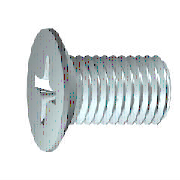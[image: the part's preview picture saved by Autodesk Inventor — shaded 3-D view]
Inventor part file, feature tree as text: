
AUTODESK INVENTOR PART (.ipt)
format: ipt  version: 2022 (Build 260153000, 153)  size: 241,664 bytes
history: native  units: mm (DEFAULTED — no unit token found)
features: sketch x1, extrude x1, plane x1
ambient origin geometry x7: Origin, YZ Plane, XZ Plane, X Axis, Y Axis, Z Axis, Center Point
bodies: Solid1 (feature_tree), Body (feature_tree)
feature tree (3):
  sketch  "Sketch1"  dims[d0=25.4mm d1=1.524mm d2=3.5052mm d3=6.0452mm d8=90.0deg d4=2.1844mm d5=3.9116mm d6=4.625123mm d7=10.821041mm d9=19.05mm d10=0.0mm d11=0.472281mm d12=0.472281mm d13=8.726646mm d14=1.524mm d15=50.8mm d45=2.1844mm d16=0.0mm d17=3.9116mm d18=45.0deg d19=1.303867mm d20=1.9558mm d21=3.9116mm d22=0.3429mm d24=0.0mm d25=0.13716mm d62=45.0deg d65=0.0mm d66=0.0mm]
  extrude  "Slot"  Depth=0.13716mm
  plane  "Work Plane2"
